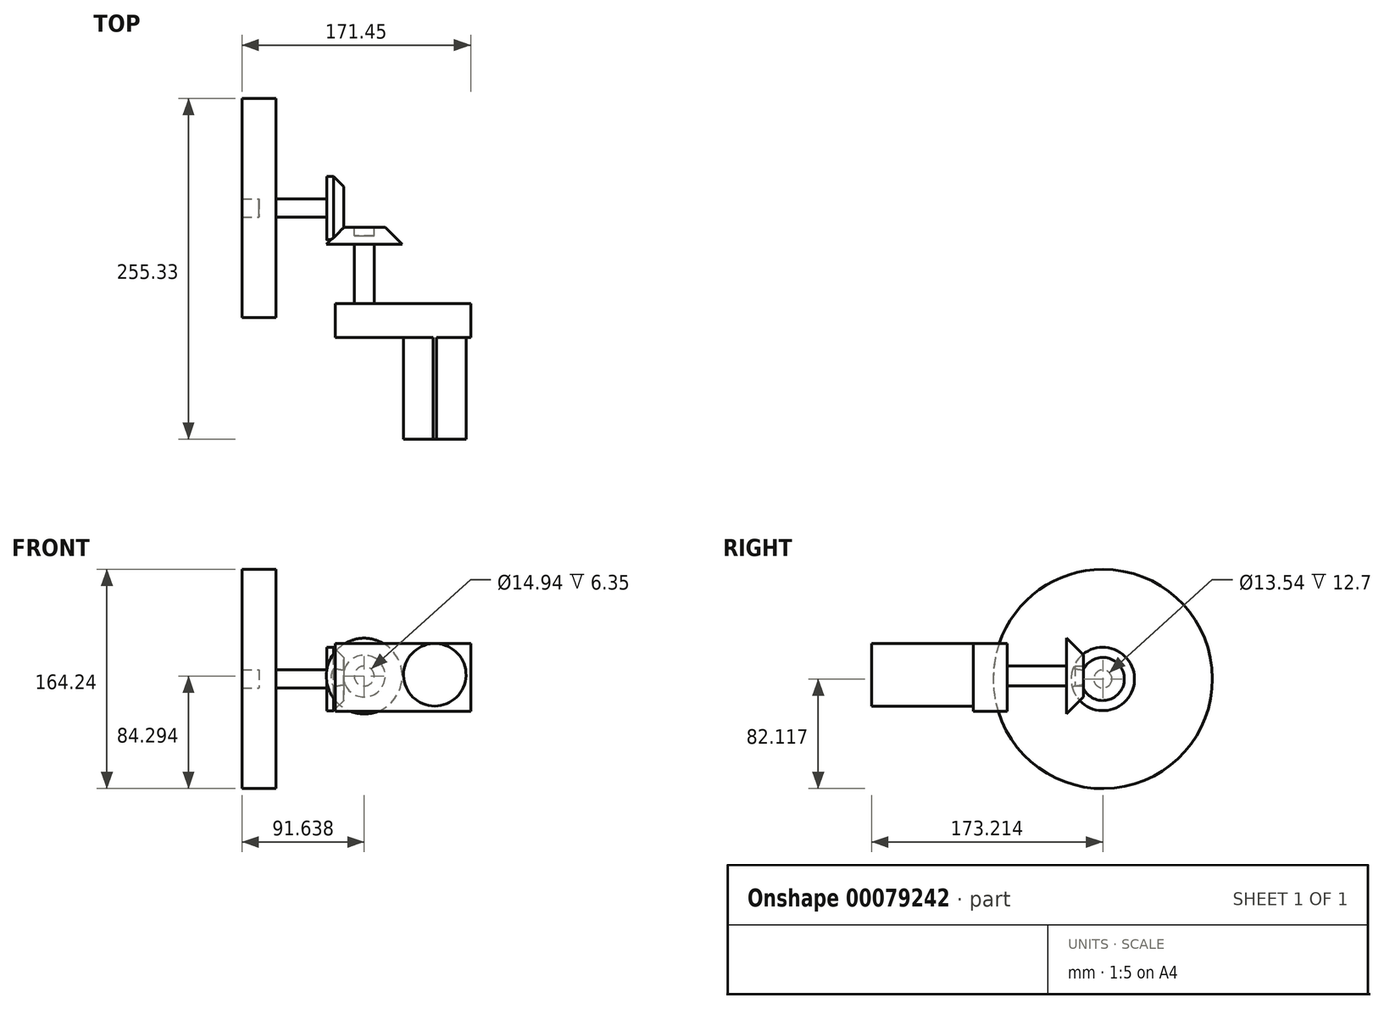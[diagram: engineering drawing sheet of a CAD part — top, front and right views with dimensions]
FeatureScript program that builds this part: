
annotation { "Feature Type Name" : "Feature", "Feature Type Description" : "" }
export const myFeature = defineFeature(function(context is Context, id is Id, definition is map)
    precondition{}
    {
        {
            var Q0;
            Q0=qCreatedBy(makeId("Front.planeOp"),FACE);
            var sketch = newSketch(context, id + "F0", { "sketchPlane" : qUnion([Q0])});
            skLineSegment(sketch, "E0.bottom", {"start": v(0, 0) * mm, "end": v(101.6, 0) * mm});
            skLineSegment(sketch, "E0.top", {"start": v(0, 50.8) * mm, "end": v(101.6, 50.8) * mm});
            skLineSegment(sketch, "E0.left", {"start": v(0, 0) * mm, "end": v(0, 50.8) * mm});
            skLineSegment(sketch, "E0.right", {"start": v(101.6, 0) * mm, "end": v(101.6, 50.8) * mm});
            skSolve(sketch);
        }
        {
            var Q0;
            Q0=makeQuery(id+"F0.imprint","IMPRINT",FACE,{"disambiguationData":[TD([[makeQuery(id+"F0.imprint","IMPRINT",EDGE,{"derivedFrom":sQuery(id+"F0.wireOp",EDGE,"E0.bottom")}),1.0]])]});
            extrude(context, id + "F1", {"entities" : qUnion([Q0]), "depth" : 25.4 * mm});
        }
        {
            var Q0;
            Q0=makeQuery(id+"F1.opExtrude","CAP_FACE",FACE,{"disambiguationData":[OSD([sQuery(id+"F0.wireOp",EDGE,"E0.bottom"),sQuery(id+"F0.wireOp",EDGE,"E0.top"),sQuery(id+"F0.wireOp",EDGE,"E0.left"),sQuery(id+"F0.wireOp",EDGE,"E0.right")])],"isStart":false});
            var sketch = newSketch(context, id + "F2", { "sketchPlane" : qUnion([Q0])});
            skCircle(sketch, "E1", {"center": v(74.7, 27.43) * mm, "radius": 23.4 * mm});
            skSolve(sketch);
        }
        {
            var Q0;
            {var subQ0=sQuery(id+"F2.wireOp",EDGE,"E1");var subQ1=makeQuery(id+"F1.opExtrude","CAP_EDGE",EDGE,{"disambiguationData":[OSD([sQuery(id+"F0.wireOp",EDGE,"E0.top")])],"isStart":false});var subQ2=makeQuery(id+"F2.imprint","INTERSECT",VERTEX,{"disambiguationData":[OD(0.0)],"derivedFrom":[subQ1,subQ0]});Q0=makeQuery(id+"F2.imprint","IMPRINT",FACE,{"disambiguationData":[TD([[makeQuery(id+"F2.imprint","IMPRINT",EDGE,{"disambiguationData":[TD([[subQ2,-1.0]])],"derivedFrom":subQ0}),1.0]])]});}
            extrude(context, id + "F3", {"entities" : qUnion([Q0]), "operationType" : NewBodyOperationType.ADD, "depth" : 76.2 * mm});
        }
        {
            var Q0;
            Q0=makeQuery(id+"F1.opExtrude","CAP_FACE",FACE,{"disambiguationData":[OSD([sQuery(id+"F0.wireOp",EDGE,"E0.bottom"),sQuery(id+"F0.wireOp",EDGE,"E0.top"),sQuery(id+"F0.wireOp",EDGE,"E0.left"),sQuery(id+"F0.wireOp",EDGE,"E0.right")])],"isStart":true});
            var sketch = newSketch(context, id + "F4", { "sketchPlane" : qUnion([Q0])});
            skCircle(sketch, "E2", {"center": v(-21.79, 26.45) * mm, "radius": 7.47 * mm});
            skSolve(sketch);
        }
        {
            var Q0;
            Q0=makeQuery(id+"F4.imprint","IMPRINT",FACE,{"disambiguationData":[TD([[makeQuery(id+"F4.imprint","IMPRINT",EDGE,{"derivedFrom":sQuery(id+"F4.wireOp",EDGE,"E2")}),1.0]])]});
            extrude(context, id + "F5", {"entities" : qUnion([Q0]), "operationType" : NewBodyOperationType.ADD, "depth" : 50.8 * mm});
        }
        {
            var Q0;
            Q0=makeQuery(id+"F5.opExtrude","CAP_FACE",FACE,{"disambiguationData":[OSD([sQuery(id+"F4.wireOp",EDGE,"E2")])],"isStart":false});
            var sketch = newSketch(context, id + "F6", { "sketchPlane" : qUnion([Q0])});
            skCircle(sketch, "E3", {"center": v(-21.79, 26.45) * mm, "radius": 28.39 * mm});
            skSolve(sketch);
        }
        {
            var Q0;
            Q0=makeQuery(id+"F6.imprint","IMPRINT",FACE,{"disambiguationData":[TD([[makeQuery(id+"F6.imprint","IMPRINT",EDGE,{"derivedFrom":sQuery(id+"F6.wireOp",EDGE,"E3")}),1.0]])]});
            extrude(context, id + "F7", {"entities" : qUnion([Q0]), "operationType" : NewBodyOperationType.ADD, "endBound" : BoundingType.SYMMETRIC, "oppositeDirection" : true, "depth" : 12.7 * mm});
        }
        {
            var Q0;
            Q0=makeQuery(id+"F7.opExtrude","CAP_EDGE",EDGE,{"disambiguationData":[OSD([sQuery(id+"F6.wireOp",EDGE,"E3")])],"isStart":true});
            chamfer(context, id + "F8", {"entities" : qUnion([Q0]), "width" : 12.7 * mm, "tangentPropagation" : true});
        }
        {
            var Q0;
            Q0=qCreatedBy(makeId("Right.planeOp"),FACE);
            var sketch = newSketch(context, id + "F9", { "sketchPlane" : qUnion([Q0])});
            skCircle(sketch, "E4", {"center": v(71.61, 24.28) * mm, "radius": 23.75 * mm});
            skPoint(sketch, "E4.first.point", {"position": v(48, 26.78) * mm});
            skPoint(sketch, "E4.second.point", {"position": v(86.62, 42.68) * mm});
            skPoint(sketch, "E4.third.point", {"position": v(90.52, 9.9) * mm});
            skSolve(sketch);
        }
        {
            var Q0;
            Q0 = qSketchRegion(id + "F9", true);
            extrude(context, id + "F10", {"entities" : qUnion([Q0]), "operationType" : NewBodyOperationType.ADD, "endBound" : BoundingType.SYMMETRIC, "depth" : 12.7 * mm});
        }
        {
            var Q0;
            Q0=makeQuery(id+"F10.opExtrude","CAP_EDGE",EDGE,{"disambiguationData":[OSD([sQuery(id+"F9.wireOp",EDGE,"E4")])],"isStart":false});
            chamfer(context, id + "F11", {"entities" : qUnion([Q0]), "width" : 7.62 * mm});
        }
        {
            var Q0;
            Q0=makeQuery(id+"F10.opExtrude","CAP_FACE",FACE,{"disambiguationData":[OSD([sQuery(id+"F9.wireOp",EDGE,"E4")])],"isStart":true});
            var sketch = newSketch(context, id + "F12", { "sketchPlane" : qUnion([Q0])});
            skCircle(sketch, "E5", {"center": v(-71.61, 24.28) * mm, "radius": 6.77 * mm});
            skSolve(sketch);
        }
        {
            var Q0;
            Q0=makeQuery(id+"F12.imprint","IMPRINT",FACE,{"disambiguationData":[TD([[makeQuery(id+"F12.imprint","IMPRINT",EDGE,{"derivedFrom":sQuery(id+"F12.wireOp",EDGE,"E5")}),1.0]])]});
            extrude(context, id + "F13", {"entities" : qUnion([Q0]), "operationType" : NewBodyOperationType.ADD, "depth" : 50.8 * mm});
        }
        {
            var Q0;
            Q0=makeQuery(id+"F13.opExtrude","CAP_FACE",FACE,{"disambiguationData":[OSD([sQuery(id+"F12.wireOp",EDGE,"E5")])],"isStart":false});
            var sketch = newSketch(context, id + "F14", { "sketchPlane" : qUnion([Q0])});
            skCircle(sketch, "E6", {"center": v(-71.61, 24.28) * mm, "radius": 82.12 * mm});
            skSolve(sketch);
        }
        {
            var Q0;
            Q0=makeQuery(id+"F14.imprint","IMPRINT",FACE,{"disambiguationData":[TD([[makeQuery(id+"F14.imprint","IMPRINT",EDGE,{"derivedFrom":sQuery(id+"F14.wireOp",EDGE,"E6")}),1.0]])]});
            extrude(context, id + "F15", {"entities" : qUnion([Q0]), "operationType" : NewBodyOperationType.ADD, "endBound" : BoundingType.SYMMETRIC, "depth" : 25.4 * mm});
        }
    });
